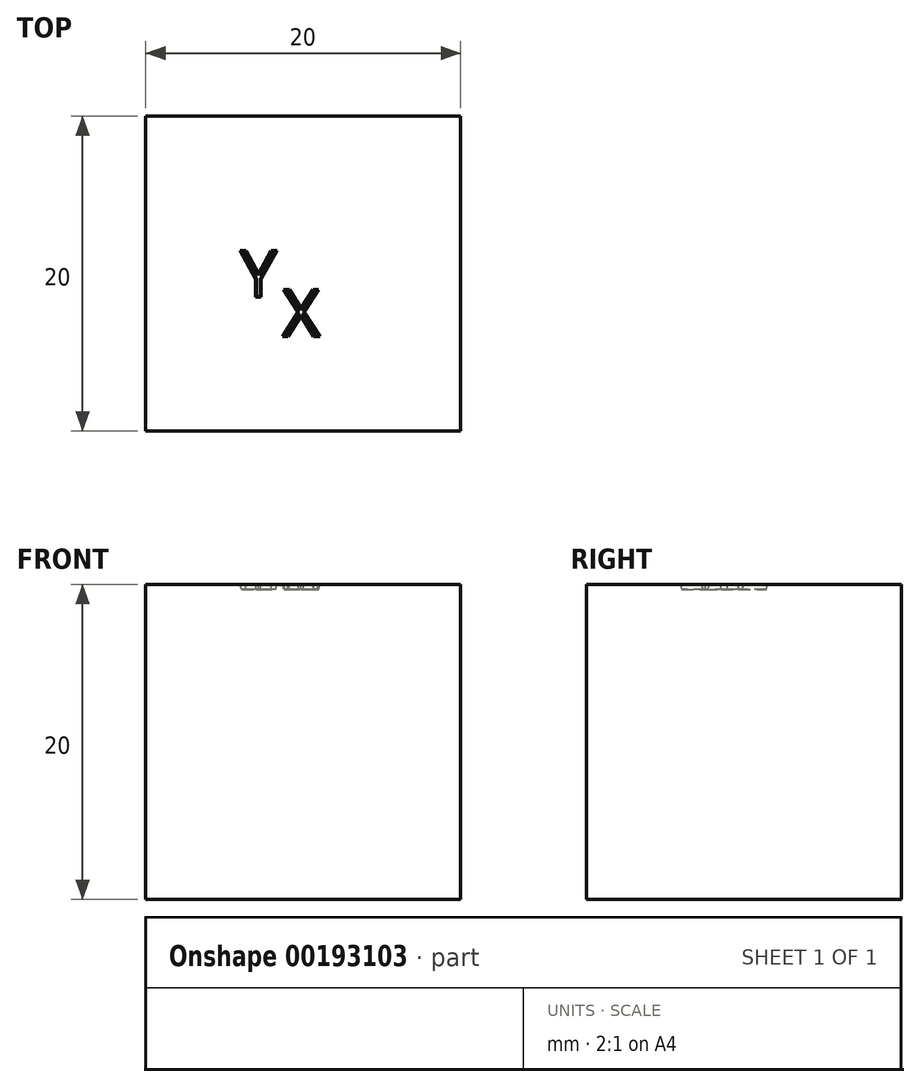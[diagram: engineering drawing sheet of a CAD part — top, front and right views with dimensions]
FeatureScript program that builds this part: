
annotation { "Feature Type Name" : "Feature", "Feature Type Description" : "" }
export const myFeature = defineFeature(function(context is Context, id is Id, definition is map)
    precondition{}
    {
        {
            var Q0;
            Q0=qCreatedBy(makeId("Top.planeOp"),FACE);
            var sketch = newSketch(context, id + "F0", { "sketchPlane" : qUnion([Q0])});
            skLineSegment(sketch, "E0.bottom", {"start": v(10, 10) * mm, "end": v(-10, 10) * mm});
            skLineSegment(sketch, "E0.top", {"start": v(10, -10) * mm, "end": v(-10, -10) * mm});
            skLineSegment(sketch, "E0.left", {"start": v(10, 10) * mm, "end": v(10, -10) * mm});
            skLineSegment(sketch, "E0.right", {"start": v(-10, 10) * mm, "end": v(-10, -10) * mm});
            skPoint(sketch, "E0.middle", {"position": v(0, 0) * mm});
            skSolve(sketch);
        }
        {
            var Q0;
            Q0 = qSketchRegion(id + "F0", true);
            extrude(context, id + "F1", {"entities" : qUnion([Q0]), "depth" : 20 * mm});
        }
        {
            var Q0;
            Q0=makeQuery(id+"F1.opExtrude","CAP_FACE",FACE,{"disambiguationData":[OSD([sQuery(id+"F0.wireOp",EDGE,"E0.bottom"),sQuery(id+"F0.wireOp",EDGE,"E0.top"),sQuery(id+"F0.wireOp",EDGE,"E0.left"),sQuery(id+"F0.wireOp",EDGE,"E0.right")])],"isStart":false});
            var sketch = newSketch(context, id + "F2", { "sketchPlane" : qUnion([Q0])});
            skText(sketch, "E1", { "text": "X", "fontName": "OpenSans-Regular.ttf"});
            skText(sketch, "E2", { "text": "Y", "fontName": "OpenSans-Regular.ttf"});
            skLineSegment(sketch, "E3", {"start": v(-4.52, 0) * mm, "end": v(-1.52, 0) * mm, "construction": true});
            const initialGuessF2  = {"E1": [-0.00133, -0.004, 1, 0, 0.003], "E2": [-0.004, -0.0015, 1, 0, 0.003]};
            skSetInitialGuess(sketch, initialGuessF2);
            skSolve(sketch);
        }
        {
            var Q0;
            Q0 = qSketchRegion(id + "F2", true);
            extrude(context, id + "F3", {"entities" : qUnion([Q0]), "operationType" : NewBodyOperationType.REMOVE, "oppositeDirection" : true, "depth" : 0.3 * mm, "hasDraft" : true, "draftAngle" : 10 * degree, "draftPullDirection" : true});
        }
    });
